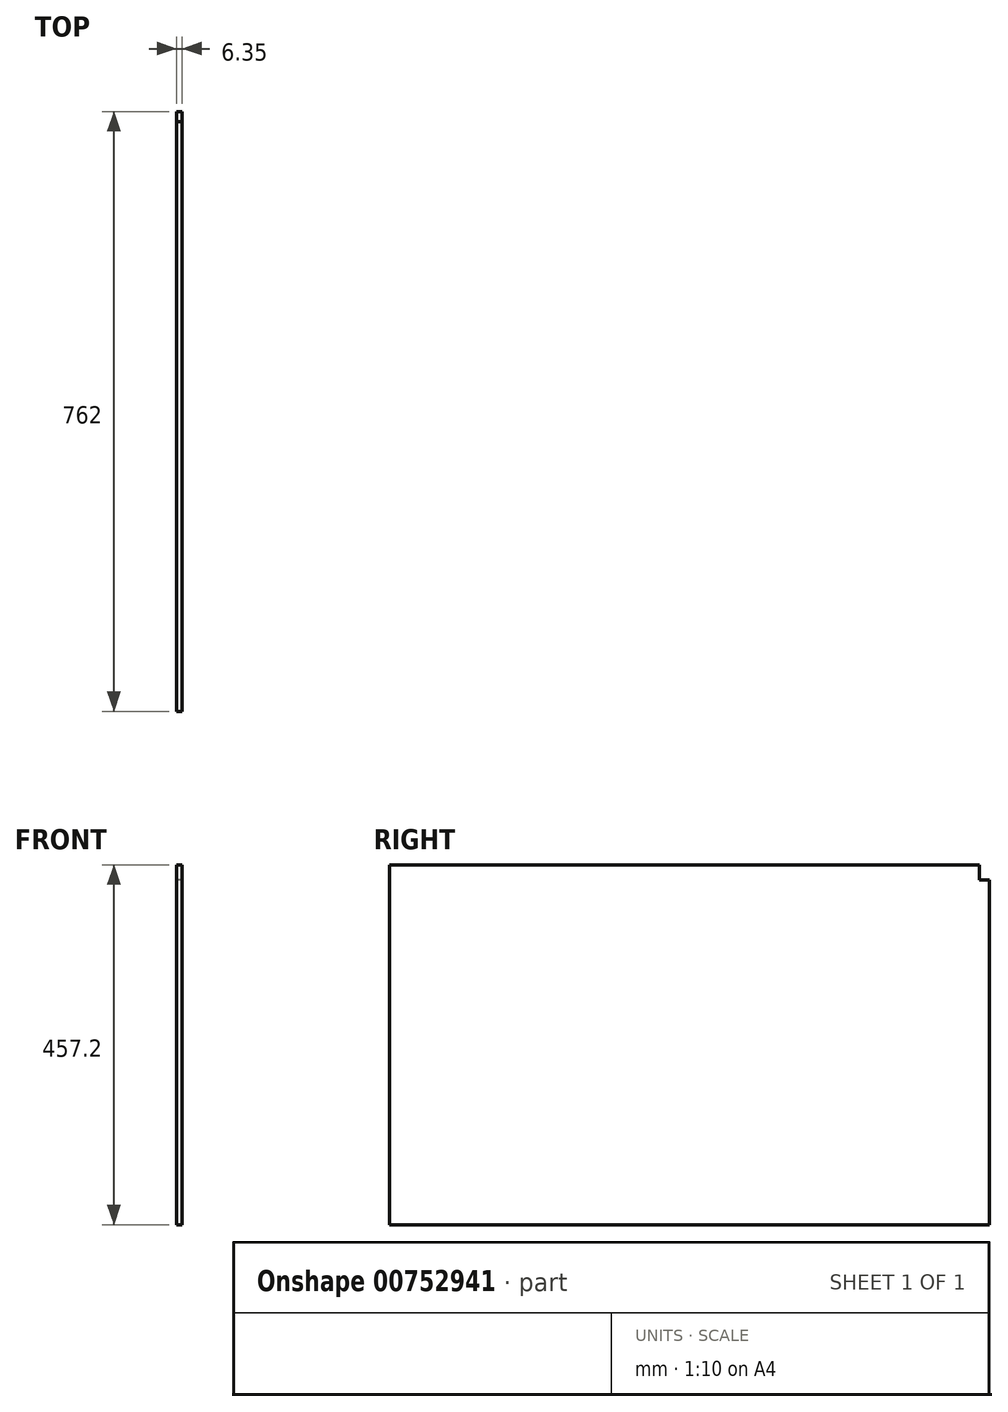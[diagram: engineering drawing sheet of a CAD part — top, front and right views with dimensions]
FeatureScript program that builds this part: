
annotation { "Feature Type Name" : "Feature", "Feature Type Description" : "" }
export const myFeature = defineFeature(function(context is Context, id is Id, definition is map)
    precondition{}
    {
        {
            var Q0;
            Q0=qCreatedBy(makeId("Front.planeOp"),FACE);
            var sketch = newSketch(context, id + "F0", { "sketchPlane" : qUnion([Q0])});
            skLineSegment(sketch, "E0.bottom", {"start": v(-6.35, 0) * mm, "end": v(0, 0) * mm});
            skLineSegment(sketch, "E0.top", {"start": v(-6.35, 457.2) * mm, "end": v(0, 457.2) * mm});
            skLineSegment(sketch, "E0.left", {"start": v(-6.35, 0) * mm, "end": v(-6.35, 457.2) * mm});
            skLineSegment(sketch, "E0.right", {"start": v(0, 0) * mm, "end": v(0, 457.2) * mm});
            skSolve(sketch);
        }
        {
            var Q0;
            Q0=makeQuery(id+"F0.imprint","IMPRINT",FACE,{"disambiguationData":[TD([[makeQuery(id+"F0.imprint","IMPRINT",EDGE,{"derivedFrom":sQuery(id+"F0.wireOp",EDGE,"E0.bottom")}),1.0]])]});
            extrude(context, id + "F1", {"entities" : qUnion([Q0]), "depth" : 762 * mm, "offsetDistance" : 25.4 * mm, "symmetric" : true});
        }
        {
            var Q0;
            Q0=makeQuery(id+"F1.opExtrude","SWEPT_FACE",FACE,{"disambiguationData":[OSD([sQuery(id+"F0.wireOp",EDGE,"E0.left")])]});
            var sketch = newSketch(context, id + "F2", { "sketchPlane" : qUnion([Q0])});
            skLineSegment(sketch, "E1.bottom", {"start": v(-381, 438.15) * mm, "end": v(-368.3, 438.15) * mm});
            skLineSegment(sketch, "E1.top", {"start": v(-381, 457.2) * mm, "end": v(-368.3, 457.2) * mm});
            skLineSegment(sketch, "E1.left", {"start": v(-381, 438.15) * mm, "end": v(-381, 457.2) * mm});
            skLineSegment(sketch, "E1.right", {"start": v(-368.3, 438.15) * mm, "end": v(-368.3, 457.2) * mm});
            skSolve(sketch);
        }
        {
            var Q0;
            Q0=makeQuery(id+"F2.imprint","IMPRINT",FACE,{"disambiguationData":[TD([[makeQuery(id+"F2.imprint","IMPRINT",EDGE,{"derivedFrom":sQuery(id+"F2.wireOp",EDGE,"E1.bottom")}),1.0]])]});
            extrude(context, id + "F3", {"entities" : qUnion([Q0]), "operationType" : NewBodyOperationType.REMOVE, "endBound" : BoundingType.THROUGH_ALL, "oppositeDirection" : true, "depth" : 25.4 * mm, "offsetDistance" : 25.4 * mm});
        }
    });
